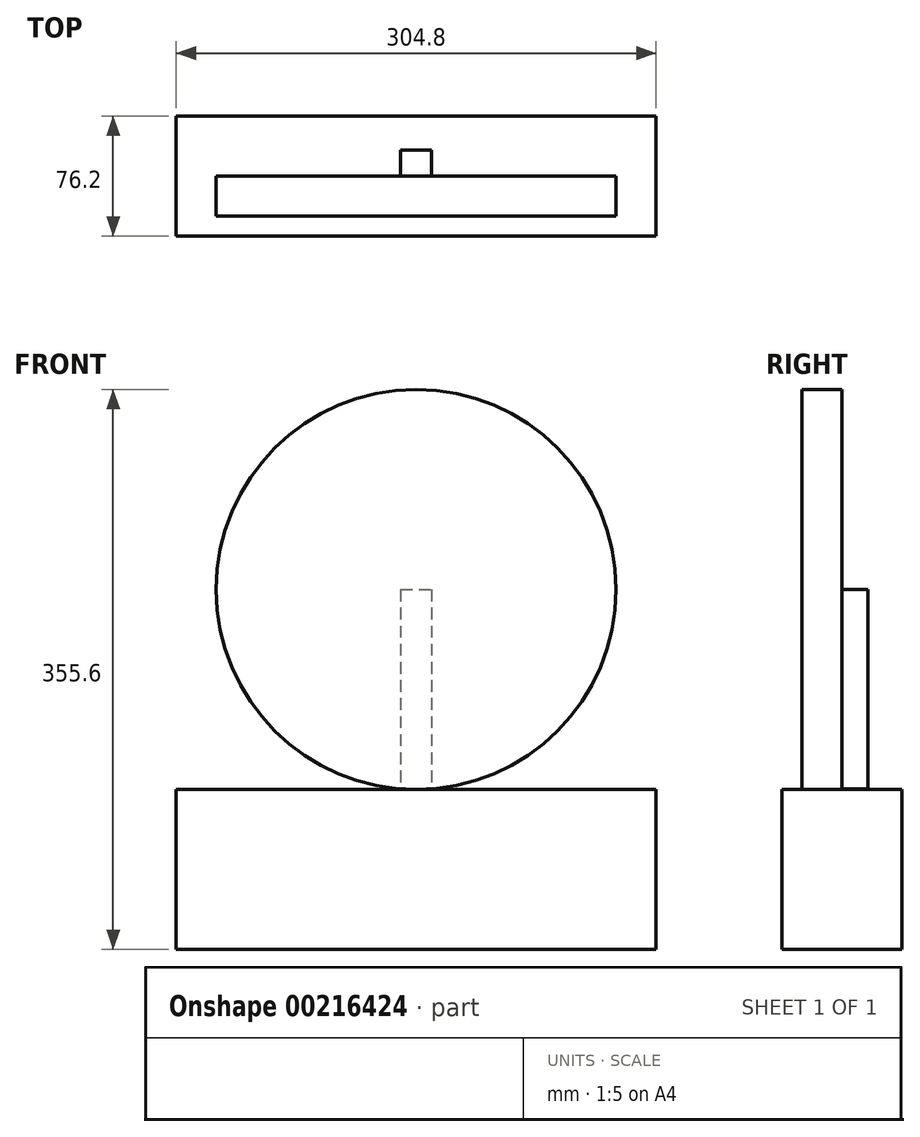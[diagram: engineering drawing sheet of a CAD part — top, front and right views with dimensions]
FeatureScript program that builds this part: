
annotation { "Feature Type Name" : "Feature", "Feature Type Description" : "" }
export const myFeature = defineFeature(function(context is Context, id is Id, definition is map)
    precondition{}
    {
        {
            var Q0;
            Q0=qCreatedBy(makeId("Front.planeOp"),FACE);
            var sketch = newSketch(context, id + "F0", { "sketchPlane" : qUnion([Q0])});
            skLineSegment(sketch, "E0.bottom", {"start": v(152.4, -101.6) * mm, "end": v(-152.4, -101.6) * mm});
            skLineSegment(sketch, "E0.top", {"start": v(152.4, 0) * mm, "end": v(-152.4, 0) * mm});
            skLineSegment(sketch, "E0.left", {"start": v(152.4, -101.6) * mm, "end": v(152.4, 0) * mm});
            skLineSegment(sketch, "E0.right", {"start": v(-152.4, -101.6) * mm, "end": v(-152.4, 0) * mm});
            skPoint(sketch, "E1.centerSnap0", {"position": v(0, 0) * mm});
            skCircle(sketch, "E2", {"center": v(0, 127) * mm, "radius": 127 * mm});
            skLineSegment(sketch, "E3", {"start": v(0, 127) * mm, "end": v(0, 0) * mm});
            skPoint(sketch, "E4", {"position": v(0, 63.5) * mm});
            skLineSegment(sketch, "E5.bottom", {"start": v(-9.82, 127) * mm, "end": v(9.82, 127) * mm});
            skLineSegment(sketch, "E5.top", {"start": v(-9.82, 0) * mm, "end": v(9.82, 0) * mm});
            skLineSegment(sketch, "E5.left", {"start": v(-9.82, 127) * mm, "end": v(-9.82, 0) * mm});
            skLineSegment(sketch, "E5.right", {"start": v(9.82, 127) * mm, "end": v(9.82, 0) * mm});
            skSolve(sketch);
        }
        {
            var Q0;
            Q0=makeQuery(id+"F0.imprint","IMPRINT",FACE,{"disambiguationData":[TD([[makeQuery(id+"F0.imprint","IMPRINT",EDGE,{"derivedFrom":sQuery(id+"F0.wireOp",EDGE,"E0.bottom")}),-1.0]])]});
            extrude(context, id + "F1", {"entities" : qUnion([Q0]), "endBound" : BoundingType.SYMMETRIC, "depth" : 76.2 * mm});
        }
        {
            var Q0;
            Q0=makeQuery(id+"F0.imprint","IMPRINT",FACE,{"disambiguationData":[TD([[makeQuery(id+"F0.imprint","IMPRINT",EDGE,{"derivedFrom":sQuery(id+"F0.wireOp",EDGE,"E2")}),1.0]])]});
            extrude(context, id + "F2", {"entities" : qUnion([Q0]), "oppositeDirection" : true, "depth" : 16.5 * mm});
        }
        {
            var Q0;
            {var subQ0=sQuery(id+"F0.wireOp",EDGE,"E5.left");var subQ3=sQuery(id+"F0.wireOp",EDGE,"E2");var subQ4=makeQuery(id+"F0.imprint","INTERSECT",VERTEX,{"derivedFrom":[subQ3,subQ0]});Q0=makeQuery(id+"F0.imprint","IMPRINT",FACE,{"disambiguationData":[TD([[makeQuery(id+"F0.imprint","IMPRINT",EDGE,{"disambiguationData":[TD([[subQ4,1.0]])],"derivedFrom":subQ3}),1.0]])]});}
            var Q1;
            {var subQ0=sQuery(id+"F0.wireOp",EDGE,"E3");Q1=makeQuery(id+"F0.imprint","IMPRINT",FACE,{"disambiguationData":[TD([[makeQuery(id+"F0.imprint","IMPRINT",EDGE,{"derivedFrom":subQ0}),-1.0]])]});}
            var Q2;
            {var subQ0=sQuery(id+"F0.wireOp",EDGE,"E3");Q2=makeQuery(id+"F0.imprint","IMPRINT",FACE,{"disambiguationData":[TD([[makeQuery(id+"F0.imprint","IMPRINT",EDGE,{"derivedFrom":subQ0}),1.0]])]});}
            extrude(context, id + "F3", {"entities" : qUnion([Q0, Q1, Q2]), "depth" : 25.4 * mm});
        }
    });
